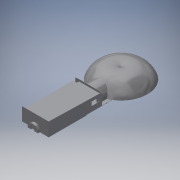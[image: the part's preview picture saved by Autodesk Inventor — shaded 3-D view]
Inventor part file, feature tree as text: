
AUTODESK INVENTOR PART (.ipt)
format: ipt  version: 2017 (Build 210142000, 142)  size: 506,368 bytes
history: native  units: in
note: dims shown in document units (in); Inventor stores cm internally (conversion verified against a paired STEP export)
features: sketch x25, extrude x24, plane x2, fillet x1, revolve x1
ambient origin geometry x8: Origin, YZ Plane, XZ Plane, XY Plane, X Axis, Y Axis, Z Axis, Center Point
bodies: Solid1 (feature_tree)
feature tree (53):
  extrude  "Extrusion1"  Depth=200.0in
  extrude  "Extrusion2"  Depth=50.0in
  extrude  "Extrusion3"  Depth=45.0in
  sketch  "Sketch4"  dims[d9=1.0in d10=0.0in d17=38.0in]
  plane  "Work Plane1"
  extrude  "Extrusion6"  Depth=38.0in
  extrude  "Extrusion9"  Depth=45.0in
  extrude  "Extrusion11"  Depth=50.0in
  fillet  "Fillet2"  Radius=74.75in
  plane  "Work Plane4"
  revolve  "Revolution1"  [1 undecoded]
  extrude  "Extrusion12"  TaperAngle=90.0deg  [1 undecoded]
  extrude  "Extrusion13"  Depth=30.0in
  extrude  "Extrusion14"  TaperAngle=90.0deg  [1 undecoded]
  extrude  "Extrusion15"  Depth=197.9375in TaperAngle=0.0deg
  extrude  "Extrusion16"  TaperAngle=180.0deg  [1 undecoded]
  extrude  "Extrusion17"  Depth=28.6in
  extrude  "Extrusion18"  Depth=36.0in TaperAngle=0.0deg
  extrude  "Extrusion19"  Depth=80.0in
  extrude  "Extrusion20"  Depth=79.0in
  extrude  "Extrusion21"  Depth=40.0in
  extrude  "Extrusion22"  Depth=39.0in
  extrude  "Extrusion23"  Depth=36.0in TaperAngle=0.0deg
  extrude  "Extrusion24"  Depth=21.0in
  extrude  "Extrusion25"  Depth=43.0in
  extrude  "Extrusion26"  Depth=36.0in TaperAngle=0.0deg
  extrude  "Extrusion27"  Depth=9.0in
  extrude  "Extrusion28"  Depth=9.0in
  extrude  "Extrusion29"  Depth=10.0in TaperAngle=0.0deg
  sketch  "Sketch1"  dims[d0=100.0in d1=200.0in]
  sketch  "Sketch2"  dims[d2=1.0in d3=0.0in d4=50.0in]
  sketch  "Sketch3"  dims[d5=1.0in d6=0.0in d8=45.0in]
  sketch  "Sketch7"  dims[d18=60.5in d19=0.0in d32=45.0in]
  sketch  "Sketch12"  dims[d33=1.0in d34=0.0in d35=50.0in d42=74.75in d43=0.0in]
  sketch  "Sketch14"  dims[d44=1.5625in d48=100.0in]
  sketch  "Sketch16"  dims[d49=43.0in d50=90.0deg]
  sketch  "Sketch18"  dims[d51=1.125in d52=30.0in]
  sketch  "Sketch19"  dims[d53=90.0deg d54=90.0deg]
  sketch  "Sketch20"  dims[d55=90.0deg d56=197.9375in d57=0.0in]
  sketch  "Sketch21"  dims[d62=40.0in d63=180.0deg]
  sketch  "Sketch22"  dims[d64=10.0in d65=0.0in d66=28.6in]
  sketch  "Sketch23"  dims[d67=65.9in d68=36.0in d69=0.0in]
  sketch  "Sketch24"  dims[d70=30.0in d71=80.0in]
  sketch  "Sketch25"  dims[d72=29.0in d73=79.0in]
  sketch  "Sketch26"  dims[d74=36.0in d75=0.0in d76=40.0in]
  sketch  "Sketch27"  dims[d77=75.0in d78=39.0in]
  sketch  "Sketch28"  dims[d79=74.0in d80=36.0in d81=0.0in]
  sketch  "Sketch29"  dims[d82=36.0in d83=0.0in d84=21.0in]
  sketch  "Sketch30"  dims[d85=43.0in d86=20.0in]
  sketch  "Sketch31"  dims[d87=42.0in d88=36.0in d89=0.0in]
  sketch  "Sketch32"  dims[d90=20.0in d91=9.0in]
  sketch  "Sketch33"  dims[d92=36.0in d93=0.0in d94=9.0in]
  sketch  "Sketch35"  dims[d95=20.0in d96=10.0in d97=0.0in d98=9.0in d99=20.0in d100=10.0in d101=0.0in d102=18.0in d103=20.0in d104=5.0in d105=0.0in d106=18.0in d107=20.0in d108=5.0in d109=0.0in d110=30.0in d111=15.0in d112=5.0in d113=0.0in d114=8.0in d115=1.0in d116=0.0in d117=100.0in d118=201.0in d119=1.0in d120=0.0in d121=1.0in d122=0.0in d123=12.25in d124=16.5in d125=5.0in d126=0.0in d127=2.0in d128=0.0in]
note: 4 required parameter values undecoded (feature->parameter linkage not recoverable at this tier; creation-order binding heuristic only, values carry confidence <= 0.55)